FCSTD DOCUMENT  (FreeCAD 0.18.4R)
Label: diff-pan-tilt-v2
License: All rights reserved
LicenseURL: http://en.wikipedia.org/wiki/All_rights_reserved
objects: Part::Cylinder×73, Part::Cut×30, Part::MultiFuse×28, Part::Box×17, Part::FeaturePython×15, Part::Part2DObjectPython×10, Part::Compound×9, Part::Fillet×8, Part::Torus×5, Part::Wedge×4, Part::Extrusion×4, Part::Sphere×3, Part::Chamfer×3, Part::Helix×2, Part::Sweep×2, App::DocumentObjectGroup×2, Part::Mirroring×2, Part::Loft×2, Part::Cone×2, Part::Feature×2, +2 more types
note: 223 computed .brp shape members not serialized (recipe doc carries the construction recipe); baked Part::Feature solids carry a one-line shape summary decoded from their .brp

FEATURE [Part::Box] Box  label="motor-plate-base"
  AttacherType = Attacher::AttachEngine3D
  Height = 3
  Length = 100
  Placement = pos=(-50,-75,32.2) rot=(0,0,1;0rad)
  Width = 150
FEATURE [Part::Cylinder] Cylinder  label="tilt-motor-opening"
  Angle = 360
  AttacherType = Attacher::AttachEngine3D
  Height = 3
  Placement = pos=(0,50,32.2) rot=(0,0,1;0rad)
  Radius = 11.25
FEATURE [Part::Cylinder] Cylinder001  label="pan-motor-opening"
  Angle = 360
  AttacherType = Attacher::AttachEngine3D
  Height = 3
  Placement = pos=(0,-50,32.2) rot=(0,0,1;0rad)
  Radius = 11.25
FEATURE [Part::Cylinder] Cylinder002  label="Cylinder"
  Angle = 360
  AttacherType = Attacher::AttachEngine3D
  Height = 3
  Radius = 1.5
FEATURE [Part::FeaturePython] Array  label="tilt-motor-screw-holes"  # Draft array (typed FeaturePython)
  Angle = 360
  ArrayType = 0
  Axis = (0,0,1)
  Base = -> Cylinder002
  Center = (0,0,0)
  Fuse = false
  IntervalAxis = (0,0,0)
  IntervalX = (31,0,0)
  IntervalY = (0,31,0)
  IntervalZ = (0,0,1)
  NumberPolar = 1
  NumberX = 2
  NumberY = 2
  NumberZ = 1
  Placement = pos=(-15.5,34.5,32.2) rot=(0,0,1;0rad)
FEATURE [Part::Cylinder] Cylinder003  label="Cylinder001"
  Angle = 360
  AttacherType = Attacher::AttachEngine3D
  Height = 3
  Radius = 1.5
FEATURE [Part::FeaturePython] Array001  label="pan-motor-screw-holes"  # Draft array (typed FeaturePython)
  Angle = 360
  ArrayType = 0
  Axis = (0,0,1)
  Base = -> Cylinder003
  Center = (0,0,0)
  Fuse = false
  IntervalAxis = (0,0,0)
  IntervalX = (31,0,0)
  IntervalY = (0,31,0)
  IntervalZ = (0,0,1)
  NumberPolar = 1
  NumberX = 2
  NumberY = 2
  NumberZ = 1
  Placement = pos=(-15.5,-65.5,32.2) rot=(0,0,1;0rad)
FEATURE [Part::Cylinder] Cylinder004  label="turret-outer"
  Angle = 360
  AttacherType = Attacher::AttachEngine3D
  Height = 35
  Placement = pos=(0,0,35.2) rot=(0,0,1;0rad)
  Radius = 20
FEATURE [Part::Part2DObjectPython] InvoluteGear  label="drive-InvoluteGear"  # Draft 2D object (typed FeaturePython)
  ExternalGear = true
  HighPrecision = true
  Modules = 1.25
  NumberOfTeeth = 60
  PressureAngle = 20
FEATURE [Part::Part2DObjectPython] InvoluteGear001  label="pinion-InvoluteGear"  # Draft 2D object (typed FeaturePython)
  ExternalGear = true
  HighPrecision = true
  Modules = 1.25
  NumberOfTeeth = 20
  PressureAngle = 20
FEATURE [Part::Part2DObjectPython] InvoluteGear002  label="drive-InvoluteGear001"  # Draft 2D object (typed FeaturePython)
  ExternalGear = true
  HighPrecision = true
  Modules = 1.25
  NumberOfTeeth = 60
  PressureAngle = 20
FEATURE [Part::Helix] Helix  label="drive-Helix"
  Angle = 0
  AttacherType = Attacher::AttachEngine3D
  Height = 5
  LocalCoord = 0
  Pitch = 300
  Radius = 1
  Style = 1
FEATURE [Part::Sweep] Sweep  label="half-base-gear-sweep"
  Frenet = true
  Sections = -> [InvoluteGear002]
  Solid = true
  Spine = -> Helix [Edge1]
  Transition = 1
FEATURE [Part::Helix] Helix001  label="pinion-Helix"
  Angle = 0
  AttacherType = Attacher::AttachEngine3D
  Height = 5
  LocalCoord = 0
  Pitch = 100
  Radius = 1
  Style = 1
FEATURE [App::DocumentObjectGroup] Group002  label="gear-templates"
  Group = -> [InvoluteGear001,InvoluteGear,Helix,Helix001]
FEATURE [Part::Part2DObjectPython] InvoluteGear003  label="pinion-InvoluteGear001"  # Draft 2D object (typed FeaturePython)
  ExternalGear = true
  HighPrecision = true
  Modules = 1.25
  NumberOfTeeth = 20
  PressureAngle = 20
FEATURE [Part::Sweep] Sweep001
  Frenet = true
  Placement = pos=(0,0,0) rot=(0,0,1;0.15708rad)
  Sections = -> [InvoluteGear003]
  Solid = true
  Spine = -> Helix001 [Edge1]
  Transition = 1
FEATURE [Part::Mirroring] Part__Mirroring001  label="Sweep001 (Mirror #2)"
  Base = (0,0,0)
  Normal = (0,0,1)
  Source = -> Sweep001
FEATURE [Part::MultiFuse] Fusion002  label="pan-pinion-base-shape"
  Placement = pos=(0,-50,43.2) rot=(0,0,1;0rad)
  Shapes = -> [Part__Mirroring001,Sweep001]
FEATURE [Part::MultiFuse] Fusion003  label="tilt-pinion-base-shape"
  Placement = pos=(0,50,54.2) rot=(0,0,1;0rad)
  Shapes = -> [Part__Mirroring001,Sweep001]
FEATURE [Part::Part2DObjectPython] InvoluteGear004  label="drive-InvoluteGear002"  # Draft 2D object (typed FeaturePython)
  ExternalGear = true
  HighPrecision = true
  Modules = 1.25
  NumberOfTeeth = 60
  PressureAngle = 20
FEATURE [Part::Part2DObjectPython] InvoluteGear005  label="drive-InvoluteGear003"  # Draft 2D object (typed FeaturePython)
  ExternalGear = true
  HighPrecision = true
  Modules = 0.983333
  NumberOfTeeth = 60
  Placement = pos=(0,0,8) rot=(0,0,1;0rad)
  PressureAngle = 20
FEATURE [Part::Loft] Loft  label="gear-Loft"
  Closed = false
  MaxDegree = 5
  Ruled = false
  Sections = -> [InvoluteGear004,InvoluteGear005]
  Solid = true
FEATURE [Part::Cone] Cone
  Angle = 360
  AttacherType = Attacher::AttachEngine3D
  Height = 8
  Radius1 = 36
  Radius2 = 44
FEATURE [Part::Cylinder] Cylinder005  label="Cylinder002"
  Angle = 360
  AttacherType = Attacher::AttachEngine3D
  Height = 8
  Radius = 44
FEATURE [Part::Cut] Cut  label="bottom-bevel-Cut"
  Base = -> Cylinder005
  Tool = -> Cone
FEATURE [Part::Cone] Cone001
  Angle = 360
  AttacherType = Attacher::AttachEngine3D
  Height = 8
  Radius1 = 36
  Radius2 = 44
FEATURE [Part::Part2DObjectPython] InvoluteGear006  label="drive-InvoluteGear004"  # Draft 2D object (typed FeaturePython)
  ExternalGear = true
  HighPrecision = true
  Modules = 0.983333
  NumberOfTeeth = 60
  Placement = pos=(0,0,8) rot=(0,0,1;0rad)
  PressureAngle = 20
FEATURE [Part::Part2DObjectPython] InvoluteGear007  label="drive-InvoluteGear005"  # Draft 2D object (typed FeaturePython)
  ExternalGear = true
  HighPrecision = true
  Modules = 1.25
  NumberOfTeeth = 60
  PressureAngle = 20
FEATURE [Part::Cylinder] Cylinder006  label="Cylinder003"
  Angle = 360
  AttacherType = Attacher::AttachEngine3D
  Height = 8
  Radius = 44
FEATURE [Part::Cut] Cut003  label="bottom-bevel-Cut001"
  Base = -> Cylinder006
  Tool = -> Cone001
FEATURE [Part::Loft] Loft001  label="gear-Loft001"
  Closed = false
  MaxDegree = 5
  Ruled = false
  Sections = -> [InvoluteGear007,InvoluteGear006]
  Solid = true
FEATURE [Part::Cut] Cut002  label="bevel-gear002-base-shape"
  Base = -> Loft001
  Placement = pos=(0,-37.5,97.7) rot=(-1,0,0;1.5708rad)
  Tool = -> Cut003
FEATURE [Part::Cylinder] Cylinder007  label="pan-pinion-base"
  Angle = 360
  AttacherType = Attacher::AttachEngine3D
  Height = 3
  Placement = pos=(0,-50,35.7) rot=(0,0,1;0rad)
  Radius = 8
FEATURE [Part::Cylinder] Cylinder008  label="pan-pinion-stepper-shaft"
  Angle = 360
  AttacherType = Attacher::AttachEngine3D
  Height = 10.4
  Placement = pos=(0,-50,35.7) rot=(0,0,1;0rad)
  Radius = 2.5
FEATURE [Part::MultiFuse] Fusion005  label="pan-pinion-with-base"
  Shapes = -> [Cylinder007,Fusion002]
FEATURE [Part::Cylinder] Cylinder009  label="tilt-pinion-stepper-shaft"
  Angle = 360
  AttacherType = Attacher::AttachEngine3D
  Height = 10.4
  Placement = pos=(0,50,35.7) rot=(0,0,1;0rad)
  Radius = 2.5
FEATURE [Part::Cylinder] Cylinder010  label="tilt-pinion-base"
  Angle = 360
  AttacherType = Attacher::AttachEngine3D
  Height = 14
  Placement = pos=(0,50,35.7) rot=(0,0,1;0rad)
  Radius = 8
FEATURE [Part::MultiFuse] Fusion006  label="tilt-pinion-with-base"
  Shapes = -> [Fusion003,Cylinder010]
FEATURE [Part::Cylinder] Cylinder011  label="turret-inner"
  Angle = 360
  AttacherType = Attacher::AttachEngine3D
  Height = 38
  Placement = pos=(0,0,32.2) rot=(0,0,1;0rad)
  Radius = 17
FEATURE [Part::Cylinder] Cylinder012  label="pan-base-gear-bed"
  Angle = 360
  AttacherType = Attacher::AttachEngine3D
  Height = 2
  Placement = pos=(0,0,35.2) rot=(0,0,1;0rad)
  Radius = 33
FEATURE [Part::Cylinder] Cylinder013  label="pan-base-gear-inner-cylinder"
  Angle = 360
  AttacherType = Attacher::AttachEngine3D
  Height = 40.1
  Placement = pos=(0,0,38.15) rot=(0,0,1;0rad)
  Radius = 20.2
FEATURE [Part::Cylinder] Cylinder014  label="pan-base-gear-outer-cylinder"
  Angle = 360
  AttacherType = Attacher::AttachEngine3D
  Height = 30.1
  Placement = pos=(0,0,48.1) rot=(0,0,1;0rad)
  Radius = 23.2
FEATURE [Part::Mirroring] Part__Mirroring  label="half-base-gear-sweep-mirror"
  Base = (0,0,0)
  Normal = (0,0,1)
  Source = -> Sweep
FEATURE [Part::MultiFuse] Fusion  label="pan-base-gear001"
  Placement = pos=(0,0,43.2) rot=(0,1,0;3.14159rad)
  Shapes = -> [Sweep,Part__Mirroring]
FEATURE [Part::MultiFuse] Fusion008  label="pan-base-gear-with-outer-shell"
  Shapes = -> [Cylinder014,Fusion]
FEATURE [Part::MultiFuse] Fusion009  label="tilt-base-gear001"
  Placement = pos=(0,0,54.2) rot=(0,1,0;3.14159rad)
  Shapes = -> [Sweep,Part__Mirroring]
FEATURE [Part::Cylinder] Cylinder016  label="tilt-base-gear-shim"
  Angle = 360
  AttacherType = Attacher::AttachEngine3D
  Height = 1.1
  Placement = pos=(0,0,59.1) rot=(0,0,1;0rad)
  Radius = 34
FEATURE [Part::Cylinder] Cylinder017  label="tilt-base-gear-shaft"
  Angle = 360
  AttacherType = Attacher::AttachEngine3D
  Height = 11.1
  Placement = pos=(0,0,49.1) rot=(0,0,1;0rad)
  Radius = 23.4
FEATURE [Part::Cylinder] Cylinder018  label="tilt-bevel-gear-shaft"
  Angle = 360
  AttacherType = Attacher::AttachEngine3D
  Height = 8
  Placement = pos=(0,0,60.2) rot=(0,0,1;0rad)
  Radius = 23.4
FEATURE [Part::Cylinder] Cylinder019  label="tilt-base-gear-screw-hole"
  Angle = 360
  AttacherType = Attacher::AttachEngine3D
  Height = 8
  Placement = pos=(28.5,0,0) rot=(0,0,1;0rad)
  Radius = 1
FEATURE [Part::FeaturePython] Array002  label="tilt-base-gear-screw-holes"  # Draft array (typed FeaturePython)
  Angle = 360
  ArrayType = 1
  Axis = (0,0,1)
  Base = -> Cylinder019
  Center = (0,0,0)
  Fuse = false
  IntervalAxis = (0,0,0)
  IntervalX = (1,0,0)
  IntervalY = (0,1,0)
  IntervalZ = (0,0,1)
  NumberPolar = 3
  NumberX = 2
  NumberY = 4
  NumberZ = 1
  Placement = pos=(0,0,52.2) rot=(0,0,1;0rad)
FEATURE [Part::Cylinder] Cylinder020  label="bevel-gear001-screw-hole"
  Angle = 360
  AttacherType = Attacher::AttachEngine3D
  Height = 6
  Placement = pos=(28.5,0,0) rot=(0,0,1;0rad)
  Radius = 1.5
FEATURE [Part::FeaturePython] Array003  label="bevel-gear001-screw-holes"  # Draft array (typed FeaturePython)
  Angle = 360
  ArrayType = 1
  Axis = (0,0,1)
  Base = -> Cylinder020
  Center = (0,0,0)
  Fuse = false
  IntervalAxis = (0,0,0)
  IntervalX = (1,0,0)
  IntervalY = (0,1,0)
  IntervalZ = (0,0,1)
  NumberPolar = 3
  NumberX = 2
  NumberY = 2
  NumberZ = 1
  Placement = pos=(0,0,60.2) rot=(0,0,1;0rad)
FEATURE [Part::Cylinder] Cylinder021  label="tilt-base-gear-screw-head-clearance"
  Angle = 360
  AttacherType = Attacher::AttachEngine3D
  Height = 2
  Placement = pos=(28.5,0,0) rot=(0,0,1;0rad)
  Radius = 3
FEATURE [Part::FeaturePython] Array004  label="tilt-base-gear-screw-heads-clearance"  # Draft array (typed FeaturePython)
  Angle = 360
  ArrayType = 1
  Axis = (0,0,1)
  Base = -> Cylinder021
  Center = (0,0,0)
  Fuse = false
  IntervalAxis = (0,0,0)
  IntervalX = (1,0,0)
  IntervalY = (0,1,0)
  IntervalZ = (0,0,1)
  NumberPolar = 3
  NumberX = 2
  NumberY = 2
  NumberZ = 1
  Placement = pos=(0,0,66.2) rot=(0,0,1;0rad)
FEATURE [Part::MultiFuse] Fusion011  label="tilt-base-gear-and-shim"
  Shapes = -> [Fusion009,Cylinder016]
FEATURE [Part::Cylinder] Cylinder023  label="turret-main-cylinder-body"
  Angle = 360
  AttacherType = Attacher::AttachEngine3D
  Height = 39.2
  Placement = pos=(0,0,68.4) rot=(0,0,1;0rad)
  Radius = 27
FEATURE [Part::Wedge] Wedge  label="turret-tilt-side-support"
  AttacherType = Attacher::AttachEngine3D
  Placement = pos=(-27,9,87.6) rot=(0,0,1;0rad)
  X2max = 46
  X2min = 8
  Xmax = 52.4
  Xmin = 1.6
  Ymax = 19.3
  Ymin = 0
  Z2max = 20
  Z2min = 0
  Zmax = 20
  Zmin = 0
FEATURE [Part::Wedge] Wedge001  label="turret-pan-side-support"
  AttacherType = Attacher::AttachEngine3D
  Placement = pos=(-27,-9,107.6) rot=(1,0,0;3.14159rad)
  X2max = 46
  X2min = 8
  Xmax = 52.4
  Xmin = 1.6
  Ymax = 19.3
  Ymin = 0
  Z2max = 20
  Z2min = 0
  Zmax = 20
  Zmin = 0
FEATURE [Part::Cylinder] Cylinder024  label="pan-base-gear-turret-screw"
  Angle = 360
  AttacherType = Attacher::AttachEngine3D
  Height = 3.2
  Placement = pos=(20,0,74.2) rot=(0,1,0;1.5708rad)
  Radius = 1
FEATURE [Part::Cylinder] Cylinder025  label="Cylinder006"
  Angle = 360
  AttacherType = Attacher::AttachEngine3D
  Height = 4
  Placement = pos=(23,0,74.2) rot=(0,1,0;1.5708rad)
  Radius = 1.5
FEATURE [Part::Cylinder] Cylinder026  label="turret-inner-cut"
  Angle = 360
  AttacherType = Attacher::AttachEngine3D
  Height = 39.2
  Placement = pos=(0,0,68.4) rot=(0,0,1;0rad)
  Radius = 23.2
FEATURE [Part::MultiFuse] Fusion012  label="turret-main-body-fusion"
  Shapes = -> [Cylinder023,Wedge,Wedge001]
FEATURE [Part::Cut] Cut012  label="turret-main-body"
  Base = -> Fusion012
  Tool = -> Cylinder026
FEATURE [Part::Cylinder] Cylinder027  label="Cylinder007"
  Angle = 360
  AttacherType = Attacher::AttachEngine3D
  Height = 1
  Placement = pos=(26,0,74.2) rot=(0,1,0;1.5708rad)
  Radius = 3
FEATURE [Part::MultiFuse] Fusion013  label="turret-screw-clearance"
  Shapes = -> [Cylinder025,Cylinder027]
FEATURE [Part::FeaturePython] Array005  label="turret-screws-clearance"  # Draft array (typed FeaturePython)
  Angle = 360
  ArrayType = 1
  Axis = (0,0,1)
  Base = -> Fusion013
  Center = (0,0,0)
  Fuse = false
  IntervalAxis = (0,0,0)
  IntervalX = (1,0,0)
  IntervalY = (0,1,0)
  IntervalZ = (0,0,1)
  NumberPolar = 3
  NumberX = 2
  NumberY = 2
  NumberZ = 1
FEATURE [Part::FeaturePython] Array006  label="pan-base-gear-turret-screws"  # Draft array (typed FeaturePython)
  Angle = 360
  ArrayType = 1
  Axis = (0,0,1)
  Base = -> Cylinder024
  Center = (0,0,0)
  Fuse = false
  IntervalAxis = (0,0,0)
  IntervalX = (1,0,0)
  IntervalY = (0,1,0)
  IntervalZ = (0,0,1)
  NumberPolar = 3
  NumberX = 2
  NumberY = 2
  NumberZ = 1
FEATURE [Part::Cylinder] Cylinder028  label="washer-Cylinder"
  Angle = 360
  AttacherType = Attacher::AttachEngine3D
  Height = 0.5
  Placement = pos=(0,10,0) rot=(0,0,1;0rad)
  Radius = 4.25
FEATURE [Part::Cylinder] Cylinder029  label="screw-Cylinder"
  Angle = 360
  AttacherType = Attacher::AttachEngine3D
  Height = 3
  Placement = pos=(10,0,0) rot=(0,0,1;0rad)
  Radius = 1.651
FEATURE [Part::RegularPolygon] RegularPolygon  label="hex-nut-polygon"
  AttacherType = Attacher::AttachEngine3D
  Circumradius = 4.5
  Polygon = 6
FEATURE [Part::Extrusion] Extrude  label="hux-nut-Extrude"
  Base = -> RegularPolygon
  Dir = (0,0,1)
  DirMode = 2
  FaceMakerClass = Part::FaceMakerBullseye
  LengthFwd = 2.381
  LengthRev = 0
  Placement = pos=(10,0,0) rot=(0,0,1;0rad)
  Solid = true
  Symmetric = false
FEATURE [Part::Cut] Cut015  label="6-32-hex-nut"
  Base = -> Extrude
  Tool = -> Cylinder029
FEATURE [Part::Cylinder] Cylinder030  label="washer-hole-Cylinder"
  Angle = 360
  AttacherType = Attacher::AttachEngine3D
  Height = 0.8
  Placement = pos=(0,10,0) rot=(0,0,1;0rad)
  Radius = 1.651
FEATURE [Part::Cut] Cut016  label="6-32-washer"
  Base = -> Cylinder028
  Tool = -> Cylinder030
FEATURE [Part::Cylinder] Cylinder031
  Angle = 360
  AttacherType = Attacher::AttachEngine3D
  Height = 25.4
  Radius = 1.651
FEATURE [Part::Sphere] Sphere002
  Angle1 = 0
  Angle2 = 90
  Angle3 = 360
  AttacherType = Attacher::AttachEngine3D
  Placement = pos=(0,0,57.15) rot=(0,0,1;0rad)
  Radius = 3
FEATURE [Part::Fillet] Fillet002  label="screw-head-Fillet002"
  Base = -> Sphere002
  Edges = 1 edges r=0.1: [Edge3]
FEATURE [Part::Box] Box002  label="Cube002"
  AttacherType = Attacher::AttachEngine3D
  Height = 2
  Length = 6
  Placement = pos=(-3,-0.5,58.2) rot=(0,0,1;0rad)
  Width = 1
FEATURE [Part::Cut] Cut017
  Base = -> Fillet002
  Placement = pos=(0,0,-31.75) rot=(0,0,1;0rad)
  Tool = -> Box002
FEATURE [Part::Chamfer] Chamfer002  label="screw-body-Chamfer002"
  Base = -> Cylinder031
  Edges = 1 edges r=0.2: [Edge3]
FEATURE [Part::MultiFuse] Fusion014  label="6-32-1.0-screw"
  Shapes = -> [Chamfer002,Cut017]
FEATURE [App::DocumentObjectGroup] Group003  label="Hardware 6-32"
  Group = -> [Cut016,Cut015,Fusion014]
FEATURE [Part::Cylinder] Cylinder022  label="bevel-gear002-axis-hole"
  Angle = 360
  AttacherType = Attacher::AttachEngine3D
  Height = 8
  Placement = pos=(0,-29.5,97.7) rot=(1,0,0;1.5708rad)
  Radius = 1.8
FEATURE [Part::Cylinder] Cylinder032  label="arm-bottom-arc"
  Angle = 360
  AttacherType = Attacher::AttachEngine3D
  Height = 3
  Placement = pos=(0,-37.5,97.7) rot=(1,0,0;1.5708rad)
  Radius = 15
FEATURE [Part::Box] Box003  label="arm"
  AttacherType = Attacher::AttachEngine3D
  Height = 55
  Length = 30
  Placement = pos=(-15,-40.5,97.7) rot=(0,0,1;0rad)
  Width = 3
FEATURE [Part::Box] Box004  label="payload-plate-base-shape"
  AttacherType = Attacher::AttachEngine3D
  Height = 4
  Length = 30
  Placement = pos=(-15,-40.5,152.7) rot=(0,0,1;0rad)
  Width = 73
FEATURE [Part::Box] Box005  label="arm-screw-block"
  AttacherType = Attacher::AttachEngine3D
  Height = 10
  Length = 30
  Placement = pos=(-15,-37.5,142.7) rot=(0,0,1;0rad)
  Width = 10
FEATURE [Part::Fillet] Fillet003  label="arm-screw-block-with-fillet"
  Base = -> Box005
  Edges = 1 edges r=5: [Edge11]
FEATURE [Part::Cylinder] Cylinder033  label="arm-bottom-arc-axis-clearance"
  Angle = 360
  AttacherType = Attacher::AttachEngine3D
  Height = 3
  Placement = pos=(0,-37.5,97.7) rot=(1,0,0;1.5708rad)
  Radius = 6
FEATURE [Part::MultiFuse] Fusion015  label="arm-body"
  Shapes = -> [Cylinder032,Box003,Fillet003]
FEATURE [Part::Cylinder] Cylinder034  label="arm-screw-hole"
  Angle = 360
  AttacherType = Attacher::AttachEngine3D
  Height = 3
  Placement = pos=(10,-37.5,97.7) rot=(1,0,0;1.5708rad)
  Radius = 1.5
FEATURE [Part::FeaturePython] Array007  label="arm-screw-holes"  # Draft array (typed FeaturePython)
  Angle = 360
  ArrayType = 1
  Axis = (0,1,0)
  Base = -> Cylinder034
  Center = (0,0,97.7)
  Fuse = false
  IntervalAxis = (0,0,0)
  IntervalX = (1,0,0)
  IntervalY = (0,1,0)
  IntervalZ = (0,0,1)
  NumberPolar = 3
  NumberX = 2
  NumberY = 2
  NumberZ = 1
FEATURE [Part::Fillet] Fillet004  label="payload-plate-with-fillet"
  Base = -> Box004
  Edges = 2 edges r=2: [Edge10,Edge12]
FEATURE [Part::Cylinder] Cylinder035  label="bevel-gear002-screw-hole"
  Angle = 360
  AttacherType = Attacher::AttachEngine3D
  Height = 8
  Placement = pos=(10,-29.5,97.7) rot=(1,0,0;1.5708rad)
  Radius = 1
FEATURE [Part::FeaturePython] Array008  label="bevel-gear002-screw-holes"  # Draft array (typed FeaturePython)
  Angle = 360
  ArrayType = 1
  Axis = (0,1,0)
  Base = -> Cylinder035
  Center = (0,0,97.7)
  Fuse = false
  IntervalAxis = (0,0,0)
  IntervalX = (1,0,0)
  IntervalY = (0,1,0)
  IntervalZ = (0,0,1)
  NumberPolar = 3
  NumberX = 2
  NumberY = 2
  NumberZ = 1
FEATURE [Part::Cylinder] Cylinder036  label="payload-plate-screw001"
  Angle = 360
  AttacherType = Attacher::AttachEngine3D
  Height = 8
  Placement = pos=(10,-33,144.7) rot=(0,0,1;0rad)
  Radius = 1
FEATURE [Part::Cylinder] Cylinder037  label="payload-plate-screw002"
  Angle = 360
  AttacherType = Attacher::AttachEngine3D
  Height = 8
  Placement = pos=(-10,-33,144.7) rot=(0,0,1;0rad)
  Radius = 1
FEATURE [Part::Compound] Compound  label="arm-payload-plate-screw-holes"
  Links = -> [Cylinder036,Cylinder037,Cylinder033,Array007]
FEATURE [Part::Cylinder] Cylinder038  label="turret-axis-hole"
  Angle = 360
  AttacherType = Attacher::AttachEngine3D
  Height = 57
  Placement = pos=(0,28.5,97.7) rot=(1,0,0;1.5708rad)
  Radius = 1.8
FEATURE [Part::Compound] Compound001  label="turret-screws-and-axis"
  Links = -> [Cylinder038,Array005]
FEATURE [Part::Cut] Cut026  label="tilt-arm"
  Base = -> Fusion015
  Tool = -> Compound
FEATURE [Part::Cylinder] Cylinder039  label="payload-plate-screw003"
  Angle = 360
  AttacherType = Attacher::AttachEngine3D
  Height = 4
  Placement = pos=(10,-33,152.7) rot=(0,0,1;0rad)
  Radius = 1.5
FEATURE [Part::Cylinder] Cylinder040  label="payload-plate-screw004"
  Angle = 360
  AttacherType = Attacher::AttachEngine3D
  Height = 4
  Placement = pos=(-10,-33,152.7) rot=(0,0,1;0rad)
  Radius = 1.5
FEATURE [Part::Cylinder] Cylinder041  label="payload-plate-screw005"
  Angle = 360
  AttacherType = Attacher::AttachEngine3D
  Height = 4
  Placement = pos=(-10,25,152.7) rot=(0,0,1;0rad)
  Radius = 1.5
FEATURE [Part::Cylinder] Cylinder042  label="payload-plate-screw006"
  Angle = 360
  AttacherType = Attacher::AttachEngine3D
  Height = 4
  Placement = pos=(10,25,152.7) rot=(0,0,1;0rad)
  Radius = 1.5
FEATURE [Part::Cylinder] Cylinder043  label="arm-support-bottom-arc"
  Angle = 360
  AttacherType = Attacher::AttachEngine3D
  Height = 3
  Placement = pos=(0,-37.5,97.7) rot=(1,0,0;1.5708rad)
  Radius = 15
FEATURE [Part::Box] Box006  label="arm-support"
  AttacherType = Attacher::AttachEngine3D
  Height = 55
  Length = 30
  Placement = pos=(-15,-40.5,97.7) rot=(0,0,1;0rad)
  Width = 3
FEATURE [Part::Box] Box007  label="arm-screw-block001"
  AttacherType = Attacher::AttachEngine3D
  Height = 10
  Length = 30
  Placement = pos=(-15,-37.5,142.7) rot=(0,0,1;0rad)
  Width = 10
FEATURE [Part::Fillet] Fillet005  label="arm-screw-block-with-fillet001"
  Base = -> Box007
  Edges = 1 edges r=5: [Edge11]
FEATURE [Part::MultiFuse] Fusion016  label="arm-support-body"
  Placement = pos=(0,-8,0) rot=(0,0,1;3.14159rad)
  Shapes = -> [Cylinder043,Box006,Fillet005]
FEATURE [Part::Cylinder] Cylinder044  label="arm-support-axis"
  Angle = 360
  AttacherType = Attacher::AttachEngine3D
  Height = 3
  Placement = pos=(0,32.5,97.7) rot=(1,0,0;1.5708rad)
  Radius = 1.8
FEATURE [Part::Cylinder] Cylinder045  label="arm-support-payload-plate-screw001"
  Angle = 360
  AttacherType = Attacher::AttachEngine3D
  Height = 8
  Placement = pos=(10,25,144.7) rot=(0,0,1;0rad)
  Radius = 1
FEATURE [Part::Cylinder] Cylinder046  label="arm-support-payload-plate-screw002"
  Angle = 360
  AttacherType = Attacher::AttachEngine3D
  Height = 8
  Placement = pos=(-10,25,144.7) rot=(0,0,1;0rad)
  Radius = 1
FEATURE [Part::Compound] Compound004  label="arm-support-screw-and-axis-holes"
  Links = -> [Cylinder044,Cylinder046,Cylinder045]
FEATURE [Part::Cut] Cut029  label="support-arm"
  Base = -> Fusion016
  Tool = -> Compound004
FEATURE [Part::Wedge] Wedge002  label="motor-plate-reinforcement001"
  AttacherType = Attacher::AttachEngine3D
  Placement = pos=(46,0,35.2) rot=(1,0,0;1.5708rad)
  X2max = 4
  X2min = 0
  Xmax = 4
  Xmin = 0
  Ymax = 5
  Ymin = 0
  Z2max = 20
  Z2min = -20
  Zmax = 65
  Zmin = -65
FEATURE [Part::Wedge] Wedge003  label="motor-plate-reinforcement002"
  AttacherType = Attacher::AttachEngine3D
  Placement = pos=(-50,0,35.2) rot=(1,0,0;1.5708rad)
  X2max = 4
  X2min = 0
  Xmax = 4
  Xmin = 0
  Ymax = 5
  Ymin = 0
  Z2max = 20
  Z2min = -20
  Zmax = 65
  Zmin = -65
FEATURE [Part::Fillet] Fillet  label="motor-plate-with-fillet"
  Base = -> Box
  Edges = 4 edges r=10: [Edge1,Edge3,Edge5,Edge7]
FEATURE [Part::MultiFuse] Fusion017  label="motor-plate-fusion"
  Shapes = -> [Fillet,Cylinder004,Cylinder012,Wedge003,Wedge002]
FEATURE [Part::Box] Box008  label="pan-pinion-shaft-d-cut"
  AttacherType = Attacher::AttachEngine3D
  Height = 10.4
  Length = 5
  Placement = pos=(-2.5,-49,35.7) rot=(0,0,1;0rad)
  Width = 1.5
FEATURE [Part::Cut] Cut031  label="pan-pinion-d-shaft"
  Base = -> Cylinder008
  Tool = -> Box008
FEATURE [Part::Box] Box009  label="tilt-pinion-shaft-d-cut"
  AttacherType = Attacher::AttachEngine3D
  Height = 10.4
  Length = 5
  Placement = pos=(-2.5,47.5,35.7) rot=(0,0,1;0rad)
  Width = 1.5
FEATURE [Part::Cut] Cut033  label="tilt-pinion-d-shaft"
  Base = -> Cylinder009
  Tool = -> Box009
FEATURE [Part::Box] Box010  label="center-plate001"
  AttacherType = Attacher::AttachEngine3D
  Height = 1
  Length = 1
  Placement = pos=(-0.5,-10,155.7) rot=(0,0,1;0rad)
  Width = 20
FEATURE [Part::Box] Box011  label="center-plate002"
  AttacherType = Attacher::AttachEngine3D
  Height = 1
  Length = 1
  Placement = pos=(10,-0.5,155.7) rot=(0,0,1;1.5708rad)
  Width = 20
FEATURE [Part::MultiFuse] Fusion018  label="payload-plate-center"
  Shapes = -> [Box011,Box010]
FEATURE [Part::Compound] Compound003  label="payload-plate-screw-holes"
  Links = -> [Cylinder039,Cylinder041,Cylinder040,Cylinder042,Fusion018]
FEATURE [Part::Cut] Cut035  label="payload-plate"
  Base = -> Fillet004
  Tool = -> Compound003
FEATURE [Part::Cut] Cut036  label="pan-pinion-with-base-and-shaft"
  Base = -> Fusion005
  Tool = -> Cut031
FEATURE [Part::Cut] Cut037  label="tilt-pinion-with-base-and-shaft"
  Base = -> Fusion006
  Tool = -> Cut033
FEATURE [Part::Part2DObjectPython] ShapeString  label="pan-ShapeString"  # Draft 2D object (typed FeaturePython)
  FontFile = <path>
  Placement = pos=(0,0,0) rot=(0,0,1;1.5708rad)
  Size = 4
  String = Pan
  Tracking = 0
FEATURE [Part::Extrusion] Extrude001  label="pan-text"
  Base = -> ShapeString
  Dir = (0,0,1)
  DirMode = 2
  FaceMakerClass = Part::FaceMakerBullseye
  LengthFwd = 1
  LengthRev = 0
  Placement = pos=(34,-59,34.2) rot=(0,0,1;0rad)
  Solid = false
  Symmetric = false
FEATURE [Part::Part2DObjectPython] ShapeString001  label="tilt-ShapeString"  # Draft 2D object (typed FeaturePython)
  FontFile = <path>
  Placement = pos=(0,0,0) rot=(0,0,1;1.5708rad)
  Size = 4
  String = Tilt
  Tracking = 0
FEATURE [Part::Extrusion] Extrude002  label="tilt-text"
  Base = -> ShapeString001
  Dir = (0,0,1)
  DirMode = 2
  FaceMakerClass = Part::FaceMakerBullseye
  LengthFwd = 1
  LengthRev = 0
  Placement = pos=(34,43,34.2) rot=(0,0,1;0rad)
  Solid = false
  Symmetric = false
FEATURE [Part::Chamfer] Chamfer  label="tilt-pinion"
  Base = -> Cut037
  Edges = 3 edges r=0.6: [Edge204,Edge205,Edge206]
FEATURE [Part::Chamfer] Chamfer003  label="pan-pinion"
  Base = -> Cut036
  Edges = 3 edges r=0.6: [Edge204,Edge205,Edge206]
FEATURE [Part::Cylinder] Cylinder047  label="pan-motor-screw-washer001"
  Angle = 360
  AttacherType = Attacher::AttachEngine3D
  Height = 1
  Placement = pos=(-15.5,-34.5,34.2) rot=(0,0,1;0rad)
  Radius = 4
FEATURE [Part::Cylinder] Cylinder048  label="pan-motor-screw-washer002"
  Angle = 360
  AttacherType = Attacher::AttachEngine3D
  Height = 1
  Placement = pos=(15.5,-34.5,34.2) rot=(0,0,1;0rad)
  Radius = 4
FEATURE [Part::Cylinder] Cylinder049  label="tilt-motor-screw-washer001"
  Angle = 360
  AttacherType = Attacher::AttachEngine3D
  Height = 1
  Placement = pos=(-15.5,34.5,34.2) rot=(0,0,1;0rad)
  Radius = 4
FEATURE [Part::Cylinder] Cylinder050  label="tilt-motor-screw-washer002"
  Angle = 360
  AttacherType = Attacher::AttachEngine3D
  Height = 1
  Placement = pos=(15.5,34.5,34.2) rot=(0,0,1;0rad)
  Radius = 4
FEATURE [Part::MultiFuse] Fusion019  label="tilt-motor-screw-and washer-holes"
  Shapes = -> [Cylinder050,Cylinder049,Array]
FEATURE [Part::MultiFuse] Fusion020  label="pan-motor-screw-and washer-holes"
  Shapes = -> [Cylinder048,Cylinder047,Array001]
FEATURE [Part::Torus] Torus  label="base-bearing-channel"
  Angle1 = -180
  Angle2 = 180
  Angle3 = 360
  AttacherType = Attacher::AttachEngine3D
  Placement = pos=(0,0,37.7) rot=(0,0,1;0rad)
  Radius1 = 28
  Radius2 = 1.5
FEATURE [Part::Compound] Compound005  label="motor-plare-holes"
  Links = -> [Fusion020,Fusion019,Cylinder,Cylinder001,Extrude001,Extrude002,Cylinder011,Torus]
FEATURE [Part::Torus] Torus001  label="pan-bearing-channel-bottom"
  Angle1 = -180
  Angle2 = 180
  Angle3 = 360
  AttacherType = Attacher::AttachEngine3D
  Placement = pos=(0,0,37.7) rot=(0,0,1;0rad)
  Radius1 = 28
  Radius2 = 1.5
FEATURE [Part::Torus] Torus002  label="pan-bearing-channel-top"
  Angle1 = -180
  Angle2 = 180
  Angle3 = 360
  AttacherType = Attacher::AttachEngine3D
  Placement = pos=(0,0,48.7) rot=(0,0,1;0rad)
  Radius1 = 28
  Radius2 = 1.5
FEATURE [Part::Sphere] Sphere  label="ball-bearing-3mm"
  Angle1 = -90
  Angle2 = 90
  Angle3 = 360
  AttacherType = Attacher::AttachEngine3D
  Placement = pos=(28,0,37.7) rot=(0,0,1;0rad)
  Radius = 1.5
FEATURE [Part::FeaturePython] Array009  label="base-to-pan-bearings"  # Draft array (typed FeaturePython)
  Angle = 360
  ArrayType = 1
  Axis = (0,0,1)
  Base = -> Sphere
  Center = (0,0,0)
  Fuse = false
  IntervalAxis = (0,0,0)
  IntervalX = (1,0,0)
  IntervalY = (0,1,0)
  IntervalZ = (0,0,1)
  NumberPolar = 58
  NumberX = 2
  NumberY = 2
  NumberZ = 1
FEATURE [Part::Torus] Torus003  label="tilt-bearing-channel"
  Angle1 = -180
  Angle2 = 180
  Angle3 = 360
  AttacherType = Attacher::AttachEngine3D
  Placement = pos=(0,0,48.7) rot=(0,0,1;0rad)
  Radius1 = 28
  Radius2 = 1.6
FEATURE [Part::Sphere] Sphere003  label="ball-bearing-3mm001"
  Angle1 = -90
  Angle2 = 90
  Angle3 = 360
  AttacherType = Attacher::AttachEngine3D
  Placement = pos=(28,0,48.7) rot=(0,0,1;0rad)
  Radius = 1.5
FEATURE [Part::FeaturePython] Array010  label="pan-to-tilt-bearings"  # Draft array (typed FeaturePython)
  Angle = 360
  ArrayType = 1
  Axis = (0,0,1)
  Base = -> Sphere003
  Center = (0,0,0)
  Fuse = false
  IntervalAxis = (0,0,0)
  IntervalX = (1,0,0)
  IntervalY = (0,1,0)
  IntervalZ = (0,0,1)
  NumberPolar = 58
  NumberX = 2
  NumberY = 2
  NumberZ = 1
FEATURE [Part::MultiFuse] Fusion021  label="pan-base-turret-interface"
  Shapes = -> [Cylinder013,Array006]
FEATURE [Part::Compound] Compound006  label="pan-base-gear-cuts"
  Links = -> [Fusion021,Torus002,Torus001]
FEATURE [Part::Cut] Cut039  label="pan-base-gear"
  Base = -> Fusion008
  Tool = -> Compound006
FEATURE [Part::Compound] Compound007  label="tilt-base-gear-cuts"
  Links = -> [Array002,Cylinder017,Torus003]
FEATURE [Part::Cut] Cut040  label="tilt-base-gear"
  Base = -> Fusion011
  Tool = -> Compound007
FEATURE [Part::Cut] Cut001  label="bevel-gear001-with-bottom-taper"
  Base = -> Loft
  Placement = pos=(0,0,60.2) rot=(0,0,1;0.05236rad)
  Tool = -> Cut
FEATURE [Part::MultiFuse] Fusion022  label="bevel-gear001-screw-clearance"
  Shapes = -> [Array003,Array004]
FEATURE [Part::Cut] Cut041  label="bevel-gear001-shaft-cut"
  Base = -> Cut001
  Tool = -> Cylinder018
FEATURE [Part::Cut] Cut042  label="bevel-gear001"
  Base = -> Cut041
  Tool = -> Fusion022
FEATURE [Part::Feature] Part__Feature004  label="pan-motor"
  Placement = pos=(0,-50,0) rot=(0,0,1;0rad)
  shape: bbox 38.9 x 38.9 x 49.5 mm, 66 faces (baked)
FEATURE [Part::Feature] Part__Feature  label="tilt-motor"
  Placement = pos=(0,50,0) rot=(0,0,1;0rad)
  shape: bbox 38.9 x 38.9 x 49.5 mm, 66 faces (baked)
FEATURE [Part::Cut] Cut043  label="base-plate"
  Base = -> Fusion017
  Tool = -> Compound005
FEATURE [Part::Cylinder] Cylinder051  label="screw-head-clerance"
  Angle = 360
  AttacherType = Attacher::AttachEngine3D
  Height = 2
  Placement = pos=(28.5,-29.5,97.7) rot=(1,0,0;1.5708rad)
  Radius = 3.5
FEATURE [Part::FeaturePython] Array011  label="screw-head-clearances"  # Draft array (typed FeaturePython)
  Angle = 360
  ArrayType = 1
  Axis = (0,1,0)
  Base = -> Cylinder051
  Center = (0,-37.5,97.7)
  Fuse = false
  IntervalAxis = (0,0,0)
  IntervalX = (1,0,0)
  IntervalY = (0,1,0)
  IntervalZ = (0,0,1)
  NumberPolar = 3
  NumberX = 2
  NumberY = 2
  NumberZ = 1
FEATURE [Part::Compound] Compound008  label="bevel-gear002-screw-and-axis-holes"
  Links = -> [Array011,Cylinder022,Array008]
FEATURE [Part::Cut] Cut044  label="bevel-gear002"
  Base = -> Cut002
  Tool = -> Compound008
FEATURE [Part::Box] Box012  label="flat-face-tilt-side"
  AttacherType = Attacher::AttachEngine3D
  Height = 20
  Length = 16
  Placement = pos=(-8,22,87.6) rot=(0,0,1;0rad)
  Width = 2
FEATURE [Part::Box] Box013  label="flat-face-pan-side"
  AttacherType = Attacher::AttachEngine3D
  Height = 20
  Length = 16
  Placement = pos=(-8,-24,87.6) rot=(0,0,1;0rad)
  Width = 2
FEATURE [Part::MultiFuse] Fusion023  label="turret-main-body-with-flats"
  Shapes = -> [Cut012,Box013,Box012]
FEATURE [Part::Cut] Cut045  label="turret"
  Base = -> Fusion023
  Tool = -> Compound001
FEATURE [Part::Cylinder] Cylinder052  label="pot-body"
  Angle = 360
  AttacherType = Attacher::AttachEngine3D
  Height = 19.5
  Radius = 10.75
FEATURE [Part::Cylinder] Cylinder053  label="pot-thread"
  Angle = 360
  AttacherType = Attacher::AttachEngine3D
  Height = 9
  Placement = pos=(0,0,19.5) rot=(0,0,1;0rad)
  Radius = 5
FEATURE [Part::Cylinder] Cylinder054  label="pot-axis"
  Angle = 360
  AttacherType = Attacher::AttachEngine3D
  Height = 11.4
  Placement = pos=(0,0,28.5) rot=(0,0,1;0rad)
  Radius = 3
FEATURE [Part::MultiFuse] Fusion024  label="pot-multiturn"
  Placement = pos=(0,0,10.7) rot=(0,0,1;0rad)
  Shapes = -> [Cylinder052,Cylinder053,Cylinder054]
FEATURE [Part::Cylinder] Cylinder055  label="body"
  Angle = 360
  AttacherType = Attacher::AttachEngine3D
  Height = 4
  Placement = pos=(0,0,2) rot=(0,0,1;0rad)
  Radius = 17
FEATURE [Part::Cylinder] Cylinder056  label="brim"
  Angle = 360
  AttacherType = Attacher::AttachEngine3D
  Height = 2
  Radius = 24
FEATURE [Part::Cylinder] Cylinder057  label="pot-thread-hole"
  Angle = 360
  AttacherType = Attacher::AttachEngine3D
  Height = 6
  Radius = 4.9
FEATURE [Part::Cylinder] Cylinder058  label="screw-hole"
  Angle = 360
  AttacherType = Attacher::AttachEngine3D
  Height = 2
  Placement = pos=(20.5,0,0) rot=(0,0,1;0rad)
  Radius = 1.4
FEATURE [Part::MultiFuse] Fusion025  label="body-and-brim"
  Shapes = -> [Cylinder055,Cylinder056]
FEATURE [Part::FeaturePython] Array012  label="screw-holes"  # Draft array (typed FeaturePython)
  Angle = 360
  ArrayType = 1
  Axis = (0,0,1)
  Base = -> Cylinder058
  Center = (0,0,0)
  Fuse = false
  IntervalAxis = (0,0,0)
  IntervalX = (1,0,0)
  IntervalY = (0,1,0)
  IntervalZ = (0,0,1)
  NumberPolar = 3
  NumberX = 2
  NumberY = 2
  NumberZ = 1
FEATURE [Part::Cut] Cut046
  Base = -> Fusion025
  Tool = -> Cylinder057
FEATURE [Part::Cut] Cut047  label="pot-mount001"
  Base = -> Cut046
  Placement = pos=(0,0,30.2) rot=(0,0,1;0rad)
  Tool = -> Array012
FEATURE [Part::Cylinder] Cylinder059  label="pos-plate"
  Angle = 360
  AttacherType = Attacher::AttachEngine3D
  Height = 5
  Placement = pos=(0,0,71.7) rot=(0,0,1;0rad)
  Radius = 20.2
FEATURE [Part::Cylinder] Cylinder060  label="pos-screw"
  Angle = 360
  AttacherType = Attacher::AttachEngine3D
  Height = 10
  Placement = pos=(10.5,0,74.2) rot=(0,1,0;1.5708rad)
  Radius = 1.2
FEATURE [Part::FeaturePython] Array013  label="pos-plate-screws"  # Draft array (typed FeaturePython)
  Angle = 360
  ArrayType = 1
  Axis = (0,0,1)
  Base = -> Cylinder060
  Center = (0,0,0)
  Fuse = false
  IntervalAxis = (0,0,0)
  IntervalX = (1,0,0)
  IntervalY = (0,1,0)
  IntervalZ = (0,0,1)
  NumberPolar = 3
  NumberX = 2
  NumberY = 2
  NumberZ = 1
FEATURE [Part::Cylinder] Cylinder061  label="pos-cylinder"
  Angle = 360
  AttacherType = Attacher::AttachEngine3D
  Height = 20
  Placement = pos=(0,0,51.7) rot=(0,0,1;0rad)
  Radius = 4
FEATURE [Part::Box] Box014  label="pos-pick"
  AttacherType = Attacher::AttachEngine3D
  Height = 3
  Length = 8
  Placement = pos=(-4,-0.5,48.7) rot=(0,0,1;0rad)
  Width = 1
FEATURE [Part::MultiFuse] Fusion026
  Shapes = -> [Cylinder059,Cylinder061,Box014]
FEATURE [Part::Cut] Cut048  label="turret-pos-pick"
  Base = -> Fusion026
  Tool = -> Array013
FEATURE [Part::Cylinder] Cylinder062  label="servo-pot-body"
  Angle = 360
  AttacherType = Attacher::AttachEngine3D
  Height = 19.5
  Radius = 13.5
FEATURE [Part::Cylinder] Cylinder063  label="servo-pot-shaft"
  Angle = 360
  AttacherType = Attacher::AttachEngine3D
  Height = 11
  Placement = pos=(0,0,19.5) rot=(0,0,1;0rad)
  Radius = 1.5
FEATURE [Part::MultiFuse] Fusion027  label="servo-pot"
  Placement = pos=(0,0,16.7) rot=(0,0,1;0rad)
  Shapes = -> [Cylinder062,Cylinder063]
FEATURE [Part::Cylinder] Cylinder064  label="axis-ext-body"
  Angle = 360
  AttacherType = Attacher::AttachEngine3D
  Height = 11
  Radius = 4
FEATURE [Part::Cylinder] Cylinder065  label="body001"
  Angle = 360
  AttacherType = Attacher::AttachEngine3D
  Height = 4
  Placement = pos=(0,0,2) rot=(0,0,1;0rad)
  Radius = 17
FEATURE [Part::Cylinder] Cylinder066  label="brim001"
  Angle = 360
  AttacherType = Attacher::AttachEngine3D
  Height = 2
  Radius = 24
FEATURE [Part::Cylinder] Cylinder067  label="pot-thread-hole001"
  Angle = 360
  AttacherType = Attacher::AttachEngine3D
  Height = 6
  Radius = 13.5
FEATURE [Part::Cylinder] Cylinder068  label="screw-hole001"
  Angle = 360
  AttacherType = Attacher::AttachEngine3D
  Height = 2
  Placement = pos=(20.5,0,0) rot=(0,0,1;0rad)
  Radius = 1.4
FEATURE [Part::MultiFuse] Fusion028  label="body-and-brim001"
  Shapes = -> [Cylinder065,Cylinder066]
FEATURE [Part::FeaturePython] Array014  label="screw-holes001"  # Draft array (typed FeaturePython)
  Angle = 360
  ArrayType = 1
  Axis = (0,0,1)
  Base = -> Cylinder068
  Center = (0,0,0)
  Fuse = false
  IntervalAxis = (0,0,0)
  IntervalX = (1,0,0)
  IntervalY = (0,1,0)
  IntervalZ = (0,0,1)
  NumberPolar = 3
  NumberX = 2
  NumberY = 2
  NumberZ = 1
FEATURE [Part::Cut] Cut049
  Base = -> Fusion028
  Tool = -> Cylinder067
FEATURE [Part::Cylinder] Cylinder069  label="axis-hole"
  Angle = 360
  AttacherType = Attacher::AttachEngine3D
  Height = 8
  Radius = 1.5
FEATURE [Part::Box] Box015  label="pick-slot"
  AttacherType = Attacher::AttachEngine3D
  Height = 3
  Length = 8.4
  Placement = pos=(-4.2,-0.6,8) rot=(0,0,1;0rad)
  Width = 1.2
FEATURE [Part::Cut] Cut051
  Base = -> Cylinder064
  Tool = -> Cylinder069
FEATURE [Part::Cut] Cut052  label="pot-axis-ext"
  Base = -> Cut051
  Placement = pos=(0,0,40.2) rot=(0,0,1;0rad)
  Tool = -> Box015
FEATURE [Part::Torus] Torus004  label="pot-rim-clip"
  Angle1 = -180
  Angle2 = 180
  Angle3 = 360
  AttacherType = Attacher::AttachEngine3D
  Placement = pos=(0,0,2.5) rot=(0,0,1;0rad)
  Radius1 = 13.5
  Radius2 = 0.6
FEATURE [Part::Cut] Cut053
  Base = -> Cut049
  Tool = -> Array014
FEATURE [Part::MultiFuse] Fusion029  label="pot-mount002"
  Placement = pos=(0,0,30.2) rot=(0,0,1;0rad)
  Shapes = -> [Cut053,Torus004]
FEATURE [Part::MultiFuse] Fusion004  label="tilt-idler"
  Placement = pos=(0,50,43.2) rot=(0,0,1;0rad)
  Shapes = -> [Part__Mirroring001,Sweep001]
FEATURE [Part::Box] Box016  label="payload-plate-base-shape001"
  AttacherType = Attacher::AttachEngine3D
  Height = 4
  Length = 30
  Placement = pos=(-15,-40.5,152.7) rot=(0,0,1;0rad)
  Width = 73
FEATURE [Part::Cylinder] Cylinder070  label="payload-plate-screw007"
  Angle = 360
  AttacherType = Attacher::AttachEngine3D
  Height = 4
  Placement = pos=(10,-33,152.7) rot=(0,0,1;0rad)
  Radius = 1.5
FEATURE [Part::Cylinder] Cylinder071  label="payload-plate-screw008"
  Angle = 360
  AttacherType = Attacher::AttachEngine3D
  Height = 4
  Placement = pos=(-10,-33,152.7) rot=(0,0,1;0rad)
  Radius = 1.5
FEATURE [Part::Cylinder] Cylinder072  label="payload-plate-screw009"
  Angle = 360
  AttacherType = Attacher::AttachEngine3D
  Height = 4
  Placement = pos=(-10,25,152.7) rot=(0,0,1;0rad)
  Radius = 1.5
FEATURE [Part::Cylinder] Cylinder073  label="payload-plate-screw010"
  Angle = 360
  AttacherType = Attacher::AttachEngine3D
  Height = 4
  Placement = pos=(10,25,152.7) rot=(0,0,1;0rad)
  Radius = 1.5
FEATURE [Part::Compound] Compound009  label="payload-plate-screw-holes001"
  Links = -> [Cylinder070,Cylinder072,Cylinder071,Cylinder073]
FEATURE [Sketcher::SketchObject] Sketch
  MapMode = 3
  Placement = pos=(0,0,0) rot=(1,0,0;1.5708rad)
  sketch-geometry (5):
    g0: LineSegment StartX=-9.5 StartY=0 StartZ=0 EndX=9.5 EndY=0 EndZ=0
    g1: LineSegment StartX=-9.5 StartY=0 StartZ=0 EndX=-9.5 EndY=1 EndZ=0
    g2: LineSegment StartX=9.5 StartY=0 StartZ=0 EndX=9.5 EndY=6.5 EndZ=0
    g3: LineSegment [constr] StartX=0 StartY=2 StartZ=0 EndX=0 EndY=0 EndZ=0
    g4: ArcOfCircle CenterX=-7.83647 CenterY=30.8214 CenterZ=0 NormalX=0 NormalY=0 NormalZ=1 AngleXU=0 Radius=29.8678 StartAngle=4.65666 EndAngle=5.33166
  constraints (15):
    c: Parallel(g0,g-1)
    c: Distance(g0) = 19
    c: Symmetric(g0,g0,g-1)
    c: Distance(g1) = 1
    c: Perpendicular(g0,g1)
    c: Distance(g2) = 6.5
    c: Coincident(g2,g0)
    c: Perpendicular(g0,g2)
    c: Distance(g3) = 2
    c: Coincident(g3,g-1)
    c: Perpendicular(g0,g3)
    c: Coincident(g1,g0)
    c: Coincident(g4,g1)
    c: Coincident(g4,g2)
    c: PointOnObject(g3,g4)
FEATURE [Part::Extrusion] Extrude004  label="webcam-cradle-base"
  Base = -> Sketch
  Dir = (0,1,0)
  DirMode = 0
  FaceMakerClass = Part::FaceMakerBullseye
  LengthFwd = 20
  LengthRev = 0
  Solid = true
  Symmetric = true
FEATURE [Part::Fillet] Fillet007  label="webcam-cradle"
  Base = -> Extrude004
  Edges = 1 edges r=0.5: [Edge5]
  Placement = pos=(0,0,156.7) rot=(0,0,1;0rad)
FEATURE [Part::Box] Box017  label="Cube"
  AttacherType = Attacher::AttachEngine3D
  Height = 5
  Length = 3
  Placement = pos=(-12.5,-10,156.7) rot=(0,0,1;0rad)
  Width = 20
FEATURE [Part::Fillet] Fillet009  label="from-stop"
  Base = -> Box017
  Edges = 1 edges r=2: [Edge2]
FEATURE [Part::MultiFuse] Fusion030
  Shapes = -> [Box016,Fillet007,Fillet009]
FEATURE [Part::Fillet] Fillet008
  Base = -> Fusion030
  Edges = 2 edges r=2: [Edge7,Edge8]
FEATURE [Part::Cut] Cut054  label="payload-plate-webcam"
  Base = -> Fillet008
  Tool = -> Compound009
note: 2 file-system paths scrubbed to <path> (originals preserved in the JSON sidecar)
